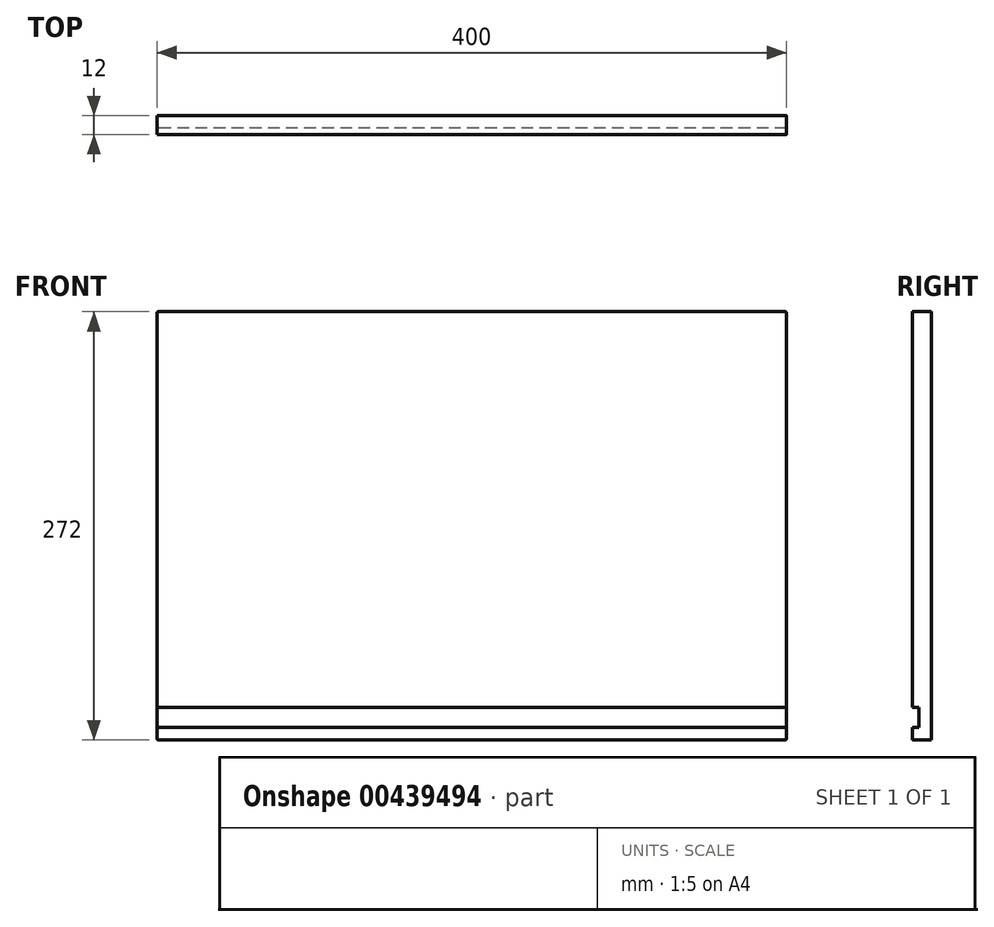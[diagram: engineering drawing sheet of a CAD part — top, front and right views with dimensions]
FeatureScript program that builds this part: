
annotation { "Feature Type Name" : "Feature", "Feature Type Description" : "" }
export const myFeature = defineFeature(function(context is Context, id is Id, definition is map)
    precondition{}
    {
        {
            var Q0;
            Q0=qCreatedBy(makeId("Right.planeOp"),FACE);
            var sketch = newSketch(context, id + "F0", { "sketchPlane" : qUnion([Q0])});
            skLineSegment(sketch, "E0", {"start": v(-12, 0) * mm, "end": v(0, 0) * mm});
            skLineSegment(sketch, "E1", {"start": v(0, 0) * mm, "end": v(0, 272) * mm});
            skLineSegment(sketch, "E2", {"start": v(0, 272) * mm, "end": v(-12, 272) * mm});
            skLineSegment(sketch, "E3", {"start": v(-12, 272) * mm, "end": v(-12, 20.5) * mm});
            skLineSegment(sketch, "E4", {"start": v(-12, 20.5) * mm, "end": v(-8, 20.5) * mm});
            skLineSegment(sketch, "E5", {"start": v(-8, 20.5) * mm, "end": v(-8, 8) * mm});
            skLineSegment(sketch, "E6", {"start": v(-8, 8) * mm, "end": v(-12, 8) * mm});
            skLineSegment(sketch, "E7", {"start": v(-12, 8) * mm, "end": v(-12, 0) * mm});
            skSolve(sketch);
        }
        {
            var Q0;
            Q0 = qSketchRegion(id + "F0", true);
            extrude(context, id + "F1", {"entities" : qUnion([Q0]), "depth" : 400 * mm, "offsetDistance" : 25 * mm, "symmetric" : true});
        }
        {
            var Q0;
            Q0=makeQuery(id+"F1.opExtrude","CAP_EDGE",EDGE,{"disambiguationData":[OSD([sQuery(id+"F0.wireOp",EDGE,"E2")])],"isStart":true});
            var Q1;
            Q1=makeQuery(id+"F1.opExtrude","CAP_EDGE",EDGE,{"disambiguationData":[OSD([sQuery(id+"F0.wireOp",EDGE,"E2")])],"isStart":false});
            var Q2;
            Q2=makeQuery(id+"F1.opExtrude","CAP_EDGE",EDGE,{"disambiguationData":[OSD([sQuery(id+"F0.wireOp",EDGE,"E0")])],"isStart":false});
            var Q3;
            Q3=makeQuery(id+"F1.opExtrude","CAP_EDGE",EDGE,{"disambiguationData":[OSD([sQuery(id+"F0.wireOp",EDGE,"E0")])],"isStart":true});
            fillet(context, id + "F2", {"entities" : qUnion([Q0, Q1, Q2, Q3]), "radius" : 1 * mm, "tangentPropagation" : true, "allowEdgeOverflow" : false});
        }
    });
